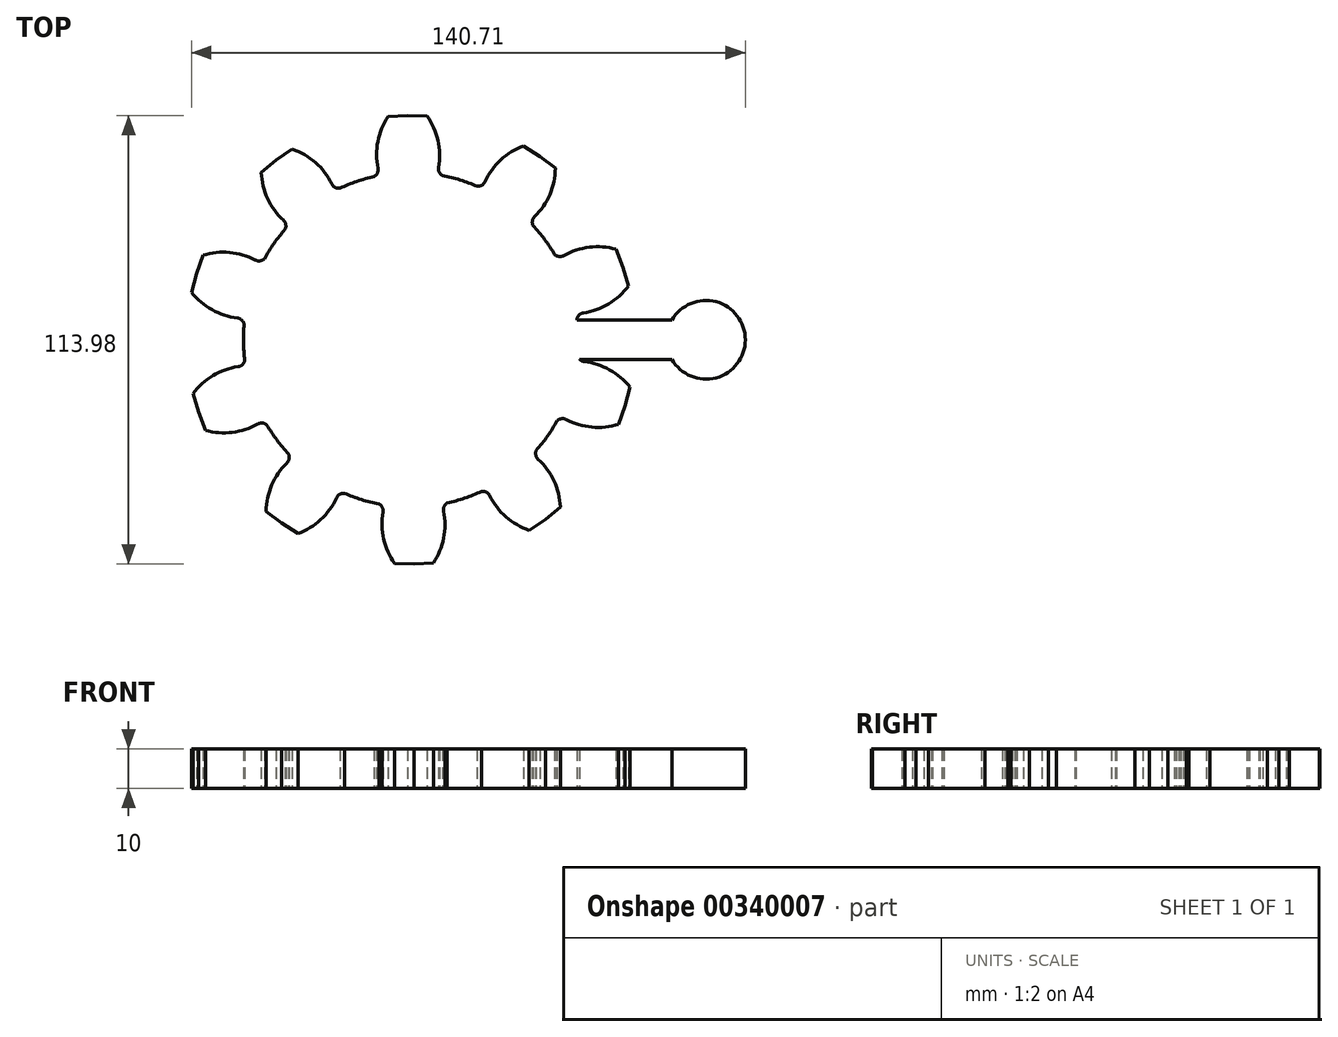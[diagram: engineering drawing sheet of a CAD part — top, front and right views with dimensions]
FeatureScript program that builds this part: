
annotation { "Feature Type Name" : "Feature", "Feature Type Description" : "" }
export const myFeature = defineFeature(function(context is Context, id is Id, definition is map)
    precondition{}
    {
        {
            assignVariable(context, id + "F0", {"name" : "Pitch", "anyValue" : 1});
        }
        {
            assignVariable(context, id + "F1", {"name" : "Diameter", "anyValue" : 10});
        }
        {
            assignVariable(context, id + "F2", {"name" : "N", "anyValue" : getVariable(context, 'Pitch') * getVariable(context, 'Diameter')});
        }
        {
            var Q0;
            Q0=qCreatedBy(makeId("Top.planeOp"),FACE);
            var sketch = newSketch(context, id + "F3", { "sketchPlane" : qUnion([Q0])});
            skCircle(sketch, "E0", {"center": v(0, 0) * mm, "radius": 10 * mm});
            skCircle(sketch, "E1", {"center": v(75, 0) * mm, "radius": 10 * mm});
            skLineSegment(sketch, "E2.bottom", {"start": v(0, -5) * mm, "end": v(75, -5) * mm});
            skLineSegment(sketch, "E2.top", {"start": v(0, 5) * mm, "end": v(75, 5) * mm});
            skLineSegment(sketch, "E2.left", {"start": v(0, -5) * mm, "end": v(0, 5) * mm});
            skLineSegment(sketch, "E2.right", {"start": v(75, -5) * mm, "end": v(75, 5) * mm});
            skSolve(sketch);
        }
        {
            var Q0;
            {var subQ5=sQuery(id+"F3.wireOp",EDGE,"E2.left");Q0=makeQuery(id+"F3.imprint","IMPRINT",FACE,{"disambiguationData":[TD([[makeQuery(id+"F3.imprint","IMPRINT",EDGE,{"derivedFrom":subQ5}),1.0]])]});}
            var Q1;
            {var subQ0=sQuery(id+"F3.wireOp",EDGE,"E2.bottom");var subQ1=sQuery(id+"F3.wireOp",EDGE,"E0");var subQ2=makeQuery(id+"F3.imprint","INTERSECT",VERTEX,{"derivedFrom":[subQ1,subQ0]});Q1=makeQuery(id+"F3.imprint","IMPRINT",FACE,{"disambiguationData":[TD([[makeQuery(id+"F3.imprint","IMPRINT",EDGE,{"disambiguationData":[TD([[subQ2,-1.0]])],"derivedFrom":subQ1}),-1.0]])]});}
            var Q2;
            {var subQ5=sQuery(id+"F3.wireOp",EDGE,"E2.right");Q2=makeQuery(id+"F3.imprint","IMPRINT",FACE,{"disambiguationData":[TD([[makeQuery(id+"F3.imprint","IMPRINT",EDGE,{"derivedFrom":subQ5}),-1.0]])]});}
            var Q3;
            {var subQ5=sQuery(id+"F3.wireOp",EDGE,"E2.right");Q3=makeQuery(id+"F3.imprint","IMPRINT",FACE,{"disambiguationData":[TD([[makeQuery(id+"F3.imprint","IMPRINT",EDGE,{"derivedFrom":subQ5}),1.0]])]});}
            var Q4;
            {var subQ5=sQuery(id+"F3.wireOp",EDGE,"E2.left");Q4=makeQuery(id+"F3.imprint","IMPRINT",FACE,{"disambiguationData":[TD([[makeQuery(id+"F3.imprint","IMPRINT",EDGE,{"derivedFrom":subQ5}),-1.0]])]});}
            extrude(context, id + "F4", {"entities" : qUnion([Q0, Q1, Q2, Q3, Q4]), "depth" : 10 * mm});
        }
        {
            var Q0;
            Q0=qCreatedBy(makeId("Top.planeOp"),FACE);
            var sketch = newSketch(context, id + "F5", { "sketchPlane" : qUnion([Q0])});
            skCircle(sketch, "E3", {"center": v(0, 0) * mm, "radius": 50 * mm, "construction": true});
            skCircle(sketch, "E4", {"center": v(0, 0) * mm, "radius": 57 * mm, "construction": true});
            skCircle(sketch, "E5", {"center": v(0, 0) * mm, "radius": 42.5 * mm});
            skCircle(sketch, "E6", {"center": v(0, 0) * mm, "radius": 46.98 * mm, "construction": true});
            skLineSegment(sketch, "E7", {"start": v(0, 0) * mm, "end": v(-8.7, 46.17) * mm, "construction": true});
            skLineSegment(sketch, "E8", {"start": v(-8.7, 46.17) * mm, "end": v(7.15, 49.16) * mm, "construction": true});
            skLineSegment(sketch, "E9", {"start": v(0, 0) * mm, "end": v(-23.74, 40.54) * mm, "construction": true});
            skLineSegment(sketch, "E10", {"start": v(-23.74, 40.54) * mm, "end": v(4.1, 56.85) * mm, "construction": true});
            skCircle(sketch, "E11", {"center": v(0, 0) * mm, "radius": 75 * mm, "construction": true});
            skLineSegment(sketch, "E12", {"start": v(0, 0) * mm, "end": v(6.65, 41.98) * mm, "construction": true});
            skCircle(sketch, "E13", {"center": v(-10.14, 46.76) * mm, "radius": 17.45 * mm, "construction": true});
            skLineSegment(sketch, "E14", {"start": v(0, 0) * mm, "end": v(10.65, 74.24) * mm, "construction": true});
            skPoint(sketch, "E15", {"position": v(7.1, 49.5) * mm});
            skLineSegment(sketch, "E16", {"start": v(0, 0) * mm, "end": v(-1.1, 75) * mm, "construction": true});
            skArc(sketch, "E17", {"start": v(7.07, 43.81) * mm, "mid": v(6.88, 50.63) * mm, "end": v(4.1, 56.85) * mm});
            skLineSegment(sketch, "E18", {"start": v(4.1, 56.85) * mm, "end": v(-0.83, 57) * mm});
            skLineSegment(sketch, "E19.MirrorCS", {"start": v(-5.76, 56.7) * mm, "end": v(-0.83, 57) * mm});
            skArc(sketch, "E20.MirrorCS", {"start": v(-8.34, 43.59) * mm, "mid": v(-8.36, 50.4) * mm, "end": v(-5.76, 56.7) * mm});
            skLineSegment(sketch, "E21", {"start": v(-9.8, 41.26) * mm, "end": v(-13.72, 40.22) * mm});
            skPoint(sketch, "E22.visualSharp", {"position": v(-7.87, 41.77) * mm});
            skArc(sketch, "E22.filletArc", {"start": v(-9.8, 41.26) * mm, "mid": v(-8.6, 42.14) * mm, "end": v(-8.34, 43.59) * mm});
            skLineSegment(sketch, "E23", {"start": v(0, 0) * mm, "end": v(-24.21, 70.98) * mm, "construction": true});
            skLineSegment(sketch, "E24", {"start": v(0, 0) * mm, "end": v(22.13, 71.66) * mm, "construction": true});
            skLineSegment(sketch, "E25", {"start": v(8.58, 41.53) * mm, "end": v(12.54, 40.6) * mm});
            skPoint(sketch, "E26.visualSharp", {"position": v(6.65, 41.98) * mm});
            skArc(sketch, "E26.filletArc", {"start": v(7.07, 43.81) * mm, "mid": v(7.37, 42.37) * mm, "end": v(8.58, 41.53) * mm});
            skSolve(sketch);
        }
        {
            var Q0;
            Q0=qCreatedBy(makeId("Front.planeOp"),FACE);
            var sketch = newSketch(context, id + "F6", { "sketchPlane" : qUnion([Q0])});
            skLineSegment(sketch, "E27", {"start": v(0, -41.37) * mm, "end": v(0, 36.54) * mm});
            skSolve(sketch);
        }
        {
            var Q0;
            {var subQ0=sQuery(id+"F5.wireOp",EDGE,"E17");Q0=makeQuery(id+"F5.imprint","IMPRINT",FACE,{"disambiguationData":[TD([[makeQuery(id+"F5.imprint","IMPRINT",EDGE,{"derivedFrom":subQ0}),1.0]])]});}
            var Q1;
            {var subQ0=sQuery(id+"F5.wireOp",EDGE,"E5");var subQ1=makeQuery(id+"F5.imprint","INTERSECT",VERTEX,{"derivedFrom":[subQ0,sQuery(id+"F5.wireOp",EDGE,"E17")]});Q1=makeQuery(id+"F5.imprint","IMPRINT",FACE,{"disambiguationData":[TD([[makeQuery(id+"F5.imprint","IMPRINT",EDGE,{"disambiguationData":[TD([[subQ1,-1.0]])],"derivedFrom":subQ0}),1.0]])]});}
            extrude(context, id + "F7", {"entities" : qUnion([Q0, Q1]), "depth" : 10 * mm});
        }
        {
            var Q0;
            Q0=makeQuery(id+"F7.opExtrude","SWEPT_BODY",BODY,{"disambiguationData":[OSD([sQuery(id+"F5.wireOp",EDGE,"E5"),sQuery(id+"F5.wireOp",EDGE,"E17"),sQuery(id+"F5.wireOp",EDGE,"E18"),sQuery(id+"F5.wireOp",EDGE,"E19.MirrorCS"),sQuery(id+"F5.wireOp",EDGE,"E20.MirrorCS")])]});
            var Q1;
            Q1=sQuery(id+"F6.wireOp",EDGE,"E27");
            circularPattern(context, id + "F8", {"operationType" : NewBodyOperationType.ADD, "entities" : qUnion([Q0]), "axis" : qUnion([Q1]), "angle" : 6.28 * radian, "instanceCount" : getVariable(context, 'N'), "equalSpace" : true});
        }
    });
